# Revit family: NACO with Louvre control
name_source: partatom
category: Windows
revit_build: Autodesk Revit 2014 (Build: 20130308_1515(x64)
units: mm (PartAtom-declared; Revit-internal decimal feet)

## types (1)
- NACO with Louvre control
    Actual_Blade_height = 312 mm
    Actual_height = 3000 mm  [stored 9.84252 ft]
    Actual_horizontal_position = 1492 mm
    Actual_width = 1500 mm  [stored 4.92126 ft]
    Actuator(Elcectric, Manual, Pneumatic) = Louvre control
    Angle_ = 75.00°
    Angle_opening = 75.00°
    Array_distance = 295 mm
    Array_visible = Yes
    B1 = 16 mm  [stored 0.0524934 ft]
    B2 = 16 mm  [stored 0.0524934 ft]
    Blade_height = 312 mm
    Blade_origin = 160 mm
    Blade_width = 1469 mm  [stored 4.81955 ft]
    Default Sill Height = 800 mm
    Depth = 46 mm  [stored 0.150919 ft]
    Frame_material = Aluminum, Anodized Silver
    Glass_material = Glass
    H1 = 12 mm  [stored 0.0393701 ft]
    H2 = 13 mm
    Height = 3000 mm  [stored 9.84252 ft]
    Main_visible = No
    No. of Blades = 10
    Numbers = 10
    PRACTICAL NUMBER OF BLADES = OKAY
    TrimProjection = 50 mm  [stored 0.164042 ft]
    Wall Closure = By host
    Width = 1500 mm  [stored 4.92126 ft]

note: [stored X ft] marks values corroborated as IEEE doubles in the binary element streams (Revit-internal decimal feet)

## geometry (parser evidence)
native form markers: Sweep x10
no freeform markers — native parametric forms only
